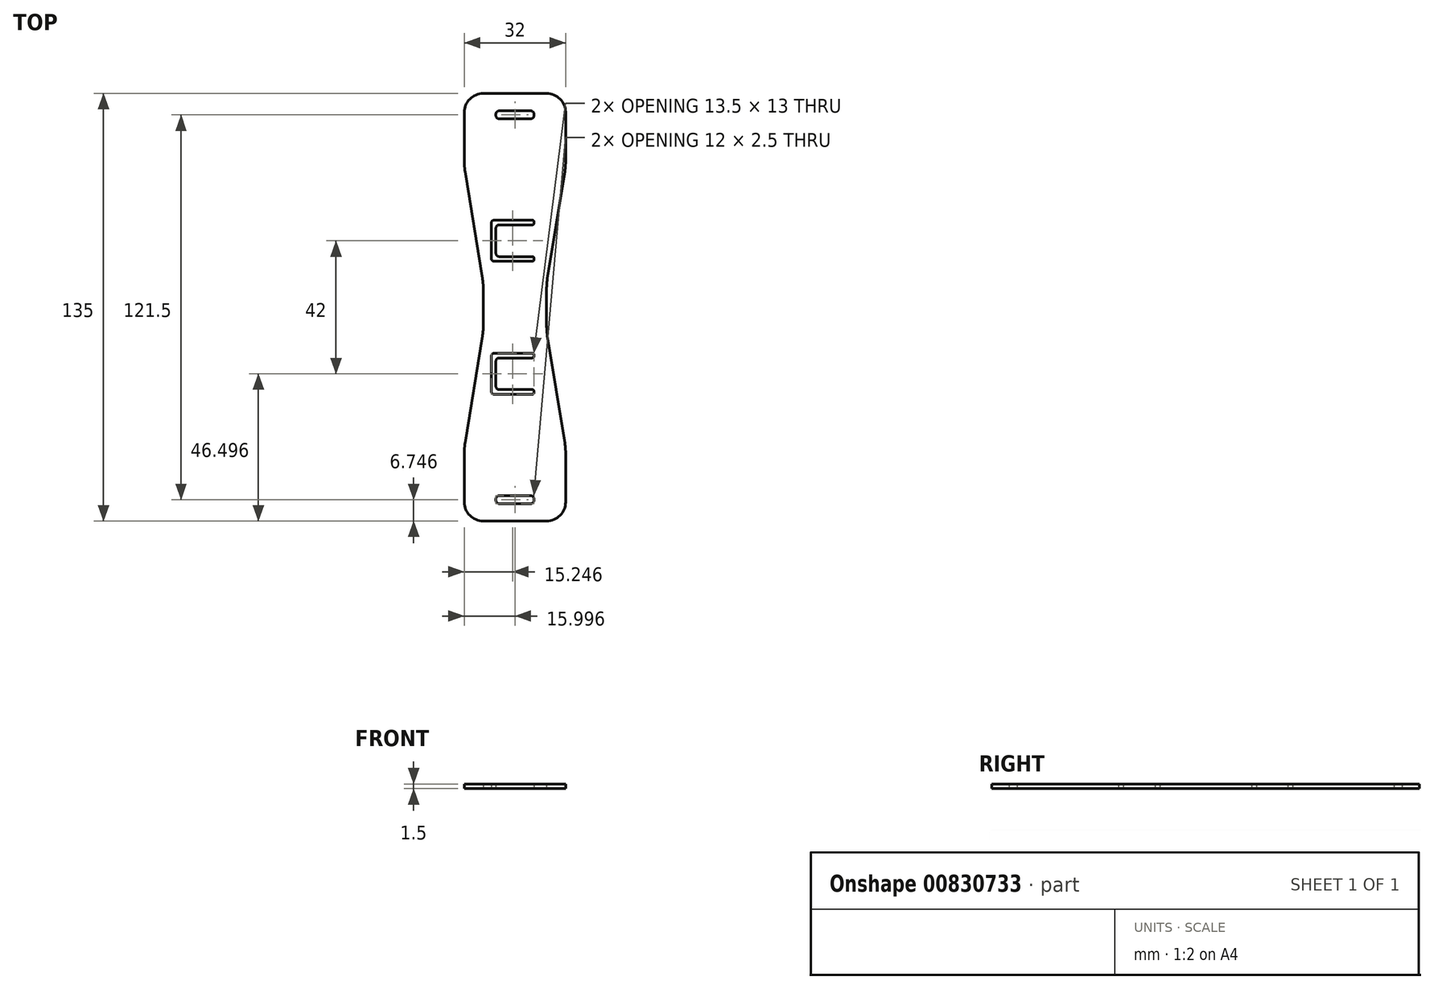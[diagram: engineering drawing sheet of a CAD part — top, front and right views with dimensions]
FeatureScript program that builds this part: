
annotation { "Feature Type Name" : "Feature", "Feature Type Description" : "" }
export const myFeature = defineFeature(function(context is Context, id is Id, definition is map)
    precondition{}
    {
        {
            var Q0;
            Q0=qCreatedBy(makeId("Top.planeOp"),FACE);
            var sketch = newSketch(context, id + "F0", { "sketchPlane" : qUnion([Q0])});
            skLineSegment(sketch, "E0.bottom", {"start": v(-15.76, 84.28) * mm, "end": v(16.24, 84.28) * mm});
            skLineSegment(sketch, "E0.top", {"start": v(-15.76, -50.72) * mm, "end": v(16.24, -50.72) * mm});
            skLineSegment(sketch, "E0.left", {"start": v(-15.76, 84.28) * mm, "end": v(-15.76, 61.28) * mm});
            skLineSegment(sketch, "E0.right", {"start": v(16.24, 84.28) * mm, "end": v(16.24, 61.28) * mm});
            skLineSegment(sketch, "E1.bottom", {"start": v(-4.76, 42.78) * mm, "end": v(5.74, 42.78) * mm});
            skLineSegment(sketch, "E1.top", {"start": v(-4.76, 32.78) * mm, "end": v(5.74, 32.78) * mm});
            skLineSegment(sketch, "E1.left", {"start": v(-5.76, 41.78) * mm, "end": v(-5.76, 33.78) * mm});
            skLineSegment(sketch, "E2.bottom", {"start": v(-4.76, 0.78) * mm, "end": v(5.74, 0.78) * mm});
            skLineSegment(sketch, "E2.top", {"start": v(-4.76, -9.22) * mm, "end": v(5.74, -9.22) * mm});
            skLineSegment(sketch, "E2.left", {"start": v(-5.76, -0.22) * mm, "end": v(-5.76, -8.22) * mm});
            skLineSegment(sketch, "E3.bottom", {"start": v(5.74, 44.28) * mm, "end": v(-6.26, 44.28) * mm});
            skLineSegment(sketch, "E3.top", {"start": v(5.74, 31.28) * mm, "end": v(-6.26, 31.28) * mm});
            skLineSegment(sketch, "E3.left", {"start": v(6.24, 43.78) * mm, "end": v(6.24, 43.28) * mm});
            skLineSegment(sketch, "E3.right", {"start": v(-7.26, 43.28) * mm, "end": v(-7.26, 32.28) * mm});
            skLineSegment(sketch, "E4.bottom", {"start": v(5.74, 2.28) * mm, "end": v(-6.26, 2.28) * mm});
            skLineSegment(sketch, "E4.top", {"start": v(5.74, -10.72) * mm, "end": v(-6.26, -10.72) * mm});
            skLineSegment(sketch, "E4.left", {"start": v(6.24, 1.78) * mm, "end": v(6.24, 1.28) * mm});
            skLineSegment(sketch, "E4.right", {"start": v(-7.26, 1.28) * mm, "end": v(-7.26, -9.72) * mm});
            skLineSegment(sketch, "E5.trimOffspring", {"start": v(6.24, 32.28) * mm, "end": v(6.24, 31.78) * mm});
            skLineSegment(sketch, "E6.trimOffspring", {"start": v(6.24, -9.72) * mm, "end": v(6.24, -10.22) * mm});
            skLineSegment(sketch, "E7.bottom", {"start": v(-4.76, -42.72) * mm, "end": v(5.24, -42.72) * mm});
            skLineSegment(sketch, "E7.top", {"start": v(-4.76, -45.22) * mm, "end": v(5.24, -45.22) * mm});
            skLineSegment(sketch, "E7.left", {"start": v(-5.76, -43.72) * mm, "end": v(-5.76, -44.22) * mm});
            skLineSegment(sketch, "E7.right", {"start": v(6.24, -43.72) * mm, "end": v(6.24, -44.22) * mm});
            skLineSegment(sketch, "E8.bottom", {"start": v(-4.76, 76.28) * mm, "end": v(5.24, 76.28) * mm});
            skLineSegment(sketch, "E8.top", {"start": v(-4.76, 78.78) * mm, "end": v(5.24, 78.78) * mm});
            skLineSegment(sketch, "E8.left", {"start": v(-5.76, 77.78) * mm, "end": v(-5.76, 77.28) * mm});
            skLineSegment(sketch, "E8.right", {"start": v(6.24, 77.78) * mm, "end": v(6.24, 77.28) * mm});
            skPoint(sketch, "E9.visualSharp", {"position": v(-5.76, 42.78) * mm});
            skArc(sketch, "E9.filletArc", {"start": v(-4.76, 42.78) * mm, "mid": v(-5.47, 42.48) * mm, "end": v(-5.76, 41.78) * mm});
            skPoint(sketch, "E10.visualSharp", {"position": v(-5.76, 32.78) * mm});
            skArc(sketch, "E10.filletArc", {"start": v(-5.76, 33.78) * mm, "mid": v(-5.47, 33.07) * mm, "end": v(-4.76, 32.78) * mm});
            skPoint(sketch, "E11.visualSharp", {"position": v(-7.26, 31.28) * mm});
            skArc(sketch, "E11.filletArc", {"start": v(-7.26, 32.28) * mm, "mid": v(-6.97, 31.57) * mm, "end": v(-6.26, 31.28) * mm});
            skPoint(sketch, "E12.visualSharp", {"position": v(-7.26, 44.28) * mm});
            skArc(sketch, "E12.filletArc", {"start": v(-6.26, 44.28) * mm, "mid": v(-6.97, 43.98) * mm, "end": v(-7.26, 43.28) * mm});
            skPoint(sketch, "E13.visualSharp", {"position": v(-5.76, -9.22) * mm});
            skArc(sketch, "E13.filletArc", {"start": v(-5.76, -8.22) * mm, "mid": v(-5.47, -8.93) * mm, "end": v(-4.76, -9.22) * mm});
            skPoint(sketch, "E14.visualSharp", {"position": v(-7.26, -10.72) * mm});
            skArc(sketch, "E14.filletArc", {"start": v(-7.26, -9.72) * mm, "mid": v(-6.97, -10.43) * mm, "end": v(-6.26, -10.72) * mm});
            skPoint(sketch, "E15.visualSharp", {"position": v(-7.26, 2.28) * mm});
            skArc(sketch, "E15.filletArc", {"start": v(-6.26, 2.28) * mm, "mid": v(-6.97, 1.98) * mm, "end": v(-7.26, 1.28) * mm});
            skPoint(sketch, "E16.visualSharp", {"position": v(-5.76, 0.78) * mm});
            skArc(sketch, "E16.filletArc", {"start": v(-4.76, 0.78) * mm, "mid": v(-5.47, 0.48) * mm, "end": v(-5.76, -0.22) * mm});
            skPoint(sketch, "E17.visualSharp", {"position": v(6.24, 0.78) * mm});
            skArc(sketch, "E17.filletArc", {"start": v(5.74, 0.78) * mm, "mid": v(6.09, 0.92) * mm, "end": v(6.24, 1.28) * mm});
            skPoint(sketch, "E18.visualSharp", {"position": v(6.24, 2.28) * mm});
            skArc(sketch, "E18.filletArc", {"start": v(6.24, 1.78) * mm, "mid": v(6.09, 2.13) * mm, "end": v(5.74, 2.28) * mm});
            skPoint(sketch, "E19.visualSharp", {"position": v(6.24, -10.72) * mm});
            skArc(sketch, "E19.filletArc", {"start": v(5.74, -10.72) * mm, "mid": v(6.09, -10.58) * mm, "end": v(6.24, -10.22) * mm});
            skPoint(sketch, "E20.visualSharp", {"position": v(6.24, -9.22) * mm});
            skArc(sketch, "E20.filletArc", {"start": v(6.24, -9.72) * mm, "mid": v(6.09, -9.37) * mm, "end": v(5.74, -9.22) * mm});
            skPoint(sketch, "E21.visualSharp", {"position": v(6.24, 42.78) * mm});
            skArc(sketch, "E21.filletArc", {"start": v(5.74, 42.78) * mm, "mid": v(6.09, 42.92) * mm, "end": v(6.24, 43.28) * mm});
            skPoint(sketch, "E22.visualSharp", {"position": v(6.24, 44.28) * mm});
            skArc(sketch, "E22.filletArc", {"start": v(6.24, 43.78) * mm, "mid": v(6.09, 44.13) * mm, "end": v(5.74, 44.28) * mm});
            skPoint(sketch, "E23.visualSharp", {"position": v(6.24, 31.28) * mm});
            skArc(sketch, "E23.filletArc", {"start": v(5.74, 31.28) * mm, "mid": v(6.09, 31.42) * mm, "end": v(6.24, 31.78) * mm});
            skPoint(sketch, "E24.visualSharp", {"position": v(6.24, 32.78) * mm});
            skArc(sketch, "E24.filletArc", {"start": v(6.24, 32.28) * mm, "mid": v(6.09, 32.63) * mm, "end": v(5.74, 32.78) * mm});
            skPoint(sketch, "E25.visualSharp", {"position": v(6.24, -42.72) * mm});
            skArc(sketch, "E25.filletArc", {"start": v(6.24, -43.72) * mm, "mid": v(5.94, -43.02) * mm, "end": v(5.24, -42.72) * mm});
            skPoint(sketch, "E26.visualSharp", {"position": v(6.24, -45.22) * mm});
            skArc(sketch, "E26.filletArc", {"start": v(5.24, -45.22) * mm, "mid": v(5.94, -44.93) * mm, "end": v(6.24, -44.22) * mm});
            skPoint(sketch, "E27.visualSharp", {"position": v(-5.76, -45.22) * mm});
            skArc(sketch, "E27.filletArc", {"start": v(-5.76, -44.22) * mm, "mid": v(-5.47, -44.93) * mm, "end": v(-4.76, -45.22) * mm});
            skPoint(sketch, "E28.visualSharp", {"position": v(-5.76, -42.72) * mm});
            skArc(sketch, "E28.filletArc", {"start": v(-4.76, -42.72) * mm, "mid": v(-5.47, -43.02) * mm, "end": v(-5.76, -43.72) * mm});
            skPoint(sketch, "E29.visualSharp", {"position": v(-5.76, 78.78) * mm});
            skArc(sketch, "E29.filletArc", {"start": v(-4.76, 78.78) * mm, "mid": v(-5.47, 78.48) * mm, "end": v(-5.76, 77.78) * mm});
            skPoint(sketch, "E30.visualSharp", {"position": v(-5.76, 76.28) * mm});
            skArc(sketch, "E30.filletArc", {"start": v(-5.76, 77.28) * mm, "mid": v(-5.47, 76.57) * mm, "end": v(-4.76, 76.28) * mm});
            skPoint(sketch, "E31.visualSharp", {"position": v(6.24, 76.28) * mm});
            skArc(sketch, "E31.filletArc", {"start": v(5.24, 76.28) * mm, "mid": v(5.94, 76.57) * mm, "end": v(6.24, 77.28) * mm});
            skPoint(sketch, "E32.visualSharp", {"position": v(6.24, 78.78) * mm});
            skArc(sketch, "E32.filletArc", {"start": v(6.24, 77.78) * mm, "mid": v(5.94, 78.48) * mm, "end": v(5.24, 78.78) * mm});
            skLineSegment(sketch, "E33", {"start": v(-15.76, 61.28) * mm, "end": v(-9.76, 24.28) * mm});
            skLineSegment(sketch, "E34", {"start": v(-9.76, 24.28) * mm, "end": v(-9.76, 9.28) * mm});
            skLineSegment(sketch, "E35", {"start": v(-9.76, 9.28) * mm, "end": v(-15.76, -27.72) * mm});
            skLineSegment(sketch, "E36", {"start": v(16.24, 61.28) * mm, "end": v(10.24, 24.28) * mm});
            skLineSegment(sketch, "E37", {"start": v(10.24, 24.28) * mm, "end": v(10.24, 9.28) * mm});
            skLineSegment(sketch, "E38", {"start": v(10.24, 9.28) * mm, "end": v(16.24, -27.72) * mm});
            skLineSegment(sketch, "E39.trimOffspring", {"start": v(16.24, -27.72) * mm, "end": v(16.24, -50.72) * mm});
            skPoint(sketch, "E40.left.end.orphan", {"position": v(-15.76, 9.28) * mm});
            skPoint(sketch, "E40.left.start.orphan", {"position": v(-15.76, 24.28) * mm});
            skLineSegment(sketch, "E41.trimOffspring", {"start": v(-15.76, -27.72) * mm, "end": v(-15.76, -50.72) * mm});
            skSolve(sketch);
        }
        {
            var Q0;
            Q0 = qSketchRegion(id + "F0", true);
            extrude(context, id + "F1", {"entities" : qUnion([Q0]), "depth" : 1.5 * mm, "offsetDistance" : 25 * mm});
        }
        {
            var Q0;
            Q0=makeQuery(id+"F1.opExtrude","SWEPT_EDGE",EDGE,{"disambiguationData":[OSD([sQuery(id+"F0.wireOp",EDGE,"E0.bottom"),sQuery(id+"F0.wireOp",EDGE,"E0.right")])]});
            var Q1;
            Q1=makeQuery(id+"F1.opExtrude","SWEPT_EDGE",EDGE,{"disambiguationData":[OSD([sQuery(id+"F0.wireOp",EDGE,"E0.bottom"),sQuery(id+"F0.wireOp",EDGE,"E0.left")])]});
            var Q2;
            Q2=makeQuery(id+"F1.opExtrude","SWEPT_EDGE",EDGE,{"disambiguationData":[OSD([sQuery(id+"F0.wireOp",EDGE,"E0.top"),sQuery(id+"F0.wireOp",EDGE,"E41.trimOffspring")])]});
            var Q3;
            Q3=makeQuery(id+"F1.opExtrude","SWEPT_EDGE",EDGE,{"disambiguationData":[OSD([sQuery(id+"F0.wireOp",EDGE,"E0.top"),sQuery(id+"F0.wireOp",EDGE,"E39.trimOffspring")])]});
            fillet(context, id + "F2", {"entities" : qUnion([Q0, Q1, Q2, Q3]), "radius" : 6 * mm, "tangentPropagation" : true, "allowEdgeOverflow" : false});
        }
        {
            var Q0;
            Q0=makeQuery(id+"F1.opExtrude","SWEPT_EDGE",EDGE,{"disambiguationData":[OSD([sQuery(id+"F0.wireOp",EDGE,"E0.right"),sQuery(id+"F0.wireOp",EDGE,"E36")])]});
            var Q1;
            Q1=makeQuery(id+"F1.opExtrude","SWEPT_EDGE",EDGE,{"disambiguationData":[OSD([sQuery(id+"F0.wireOp",EDGE,"E0.left"),sQuery(id+"F0.wireOp",EDGE,"E33")])]});
            var Q2;
            Q2=makeQuery(id+"F1.opExtrude","SWEPT_EDGE",EDGE,{"disambiguationData":[OSD([sQuery(id+"F0.wireOp",EDGE,"E38"),sQuery(id+"F0.wireOp",EDGE,"E39.trimOffspring")])]});
            var Q3;
            Q3=makeQuery(id+"F1.opExtrude","SWEPT_EDGE",EDGE,{"disambiguationData":[OSD([sQuery(id+"F0.wireOp",EDGE,"E35"),sQuery(id+"F0.wireOp",EDGE,"E41.trimOffspring")])]});
            var Q4;
            Q4=makeQuery(id+"F1.opExtrude","SWEPT_EDGE",EDGE,{"disambiguationData":[OSD([sQuery(id+"F0.wireOp",EDGE,"E34"),sQuery(id+"F0.wireOp",EDGE,"E35")])]});
            var Q5;
            Q5=makeQuery(id+"F1.opExtrude","SWEPT_EDGE",EDGE,{"disambiguationData":[OSD([sQuery(id+"F0.wireOp",EDGE,"E37"),sQuery(id+"F0.wireOp",EDGE,"E38")])]});
            var Q6;
            Q6=makeQuery(id+"F1.opExtrude","SWEPT_EDGE",EDGE,{"disambiguationData":[OSD([sQuery(id+"F0.wireOp",EDGE,"E36"),sQuery(id+"F0.wireOp",EDGE,"E37")])]});
            var Q7;
            Q7=makeQuery(id+"F1.opExtrude","SWEPT_EDGE",EDGE,{"disambiguationData":[OSD([sQuery(id+"F0.wireOp",EDGE,"E33"),sQuery(id+"F0.wireOp",EDGE,"E34")])]});
            fillet(context, id + "F3", {"entities" : qUnion([Q0, Q1, Q2, Q3, Q4, Q5, Q6, Q7]), "radius" : 20 * mm, "tangentPropagation" : true, "allowEdgeOverflow" : false});
        }
    });
